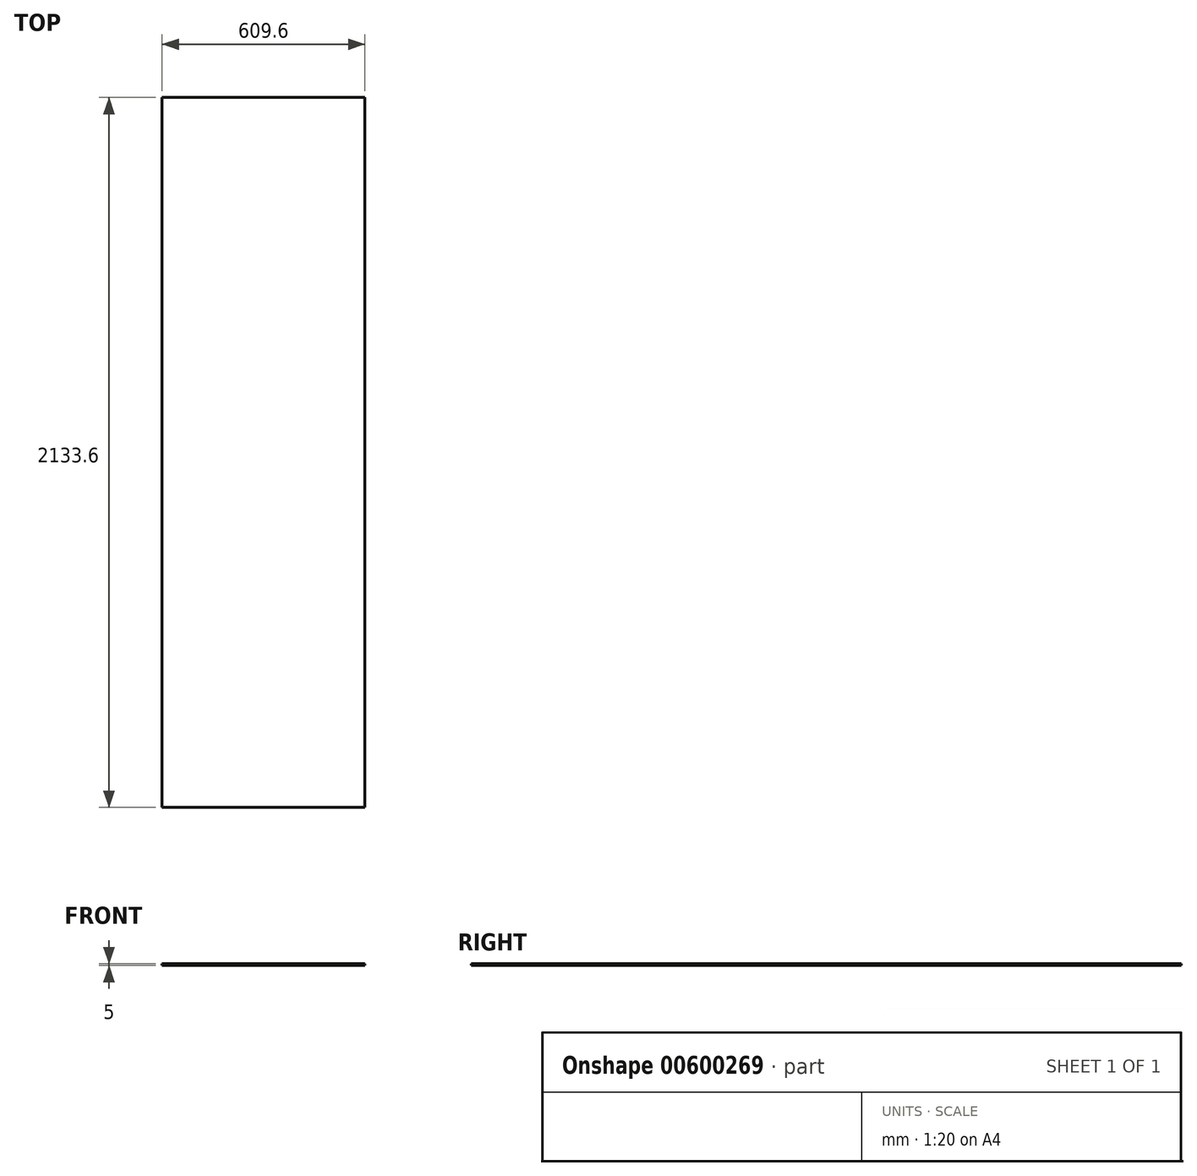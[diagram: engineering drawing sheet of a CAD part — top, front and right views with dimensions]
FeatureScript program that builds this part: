
annotation { "Feature Type Name" : "Feature", "Feature Type Description" : "" }
export const myFeature = defineFeature(function(context is Context, id is Id, definition is map)
    precondition{}
    {
        {
            var Q0;
            Q0=qCreatedBy(makeId("Front.planeOp"),FACE);
            var sketch = newSketch(context, id + "F0", { "sketchPlane" : qUnion([Q0])});
            skLineSegment(sketch, "E0", {"start": v(-39.68, 0) * mm, "end": v(-39.68, 5) * mm});
            skLineSegment(sketch, "E1", {"start": v(-39.68, 5) * mm, "end": v(569.92, 5) * mm});
            skLineSegment(sketch, "E2", {"start": v(569.92, 5) * mm, "end": v(569.92, 0) * mm});
            skLineSegment(sketch, "E3", {"start": v(569.92, 0) * mm, "end": v(-39.68, 0) * mm});
            skSolve(sketch);
        }
        {
            var Q0;
            Q0=makeQuery(id+"F0.imprint","IMPRINT",FACE,{"disambiguationData":[TD([[makeQuery(id+"F0.imprint","IMPRINT",EDGE,{"derivedFrom":sQuery(id+"F0.wireOp",EDGE,"E0")}),-1.0]])]});
            extrude(context, id + "F1", {"entities" : qUnion([Q0]), "oppositeDirection" : true, "depth" : 2133.6 * mm, "offsetDistance" : 25.4 * mm});
        }
    });
